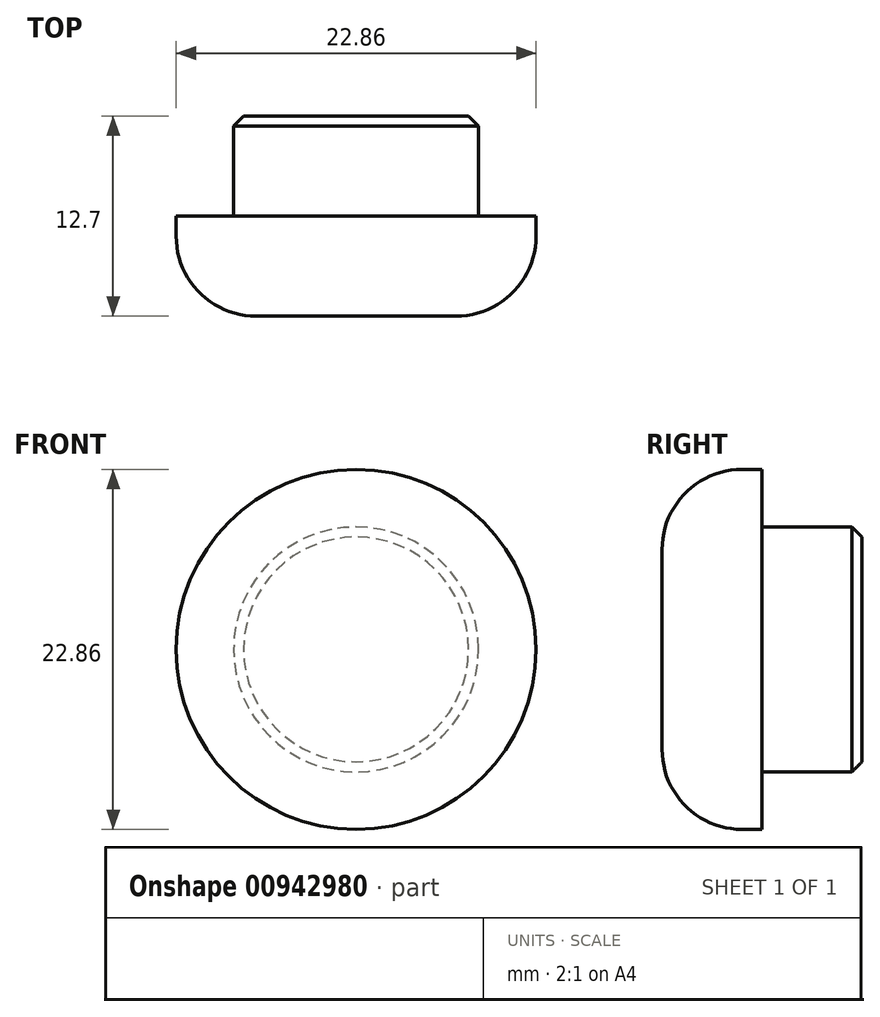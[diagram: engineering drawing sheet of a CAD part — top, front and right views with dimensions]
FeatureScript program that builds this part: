
annotation { "Feature Type Name" : "Feature", "Feature Type Description" : "" }
export const myFeature = defineFeature(function(context is Context, id is Id, definition is map)
    precondition{}
    {
        {
            var Q0;
            Q0=qCreatedBy(makeId("Front.planeOp"),FACE);
            var sketch = newSketch(context, id + "F0", { "sketchPlane" : qUnion([Q0])});
            skCircle(sketch, "E0", {"center": v(25.48, 31.94) * mm, "radius": 7.78 * mm});
            skLineSegment(sketch, "E1", {"start": v(25.48, 31.94) * mm, "end": v(25.48, 39.72) * mm});
            skLineSegment(sketch, "E2", {"start": v(25.48, 39.72) * mm, "end": v(25.48, 24.17) * mm});
            skCircle(sketch, "E3", {"center": v(25.48, 31.94) * mm, "radius": 11.43 * mm});
            skLineSegment(sketch, "E4", {"start": v(25.48, 31.94) * mm, "end": v(36.9, 31.94) * mm});
            skLineSegment(sketch, "E5", {"start": v(36.9, 31.94) * mm, "end": v(25.48, 31.94) * mm});
            skLineSegment(sketch, "E6", {"start": v(25.48, 31.94) * mm, "end": v(14.05, 31.94) * mm});
            skSolve(sketch);
        }
        {
            var Q0;
            {var subQ0=sQuery(id+"F0.wireOp",EDGE,"E1");Q0=makeQuery(id+"F0.imprint","IMPRINT",FACE,{"disambiguationData":[TD([[makeQuery(id+"F0.imprint","IMPRINT",EDGE,{"derivedFrom":subQ0}),1.0]])]});}
            var Q1;
            {var subQ0=sQuery(id+"F0.wireOp",EDGE,"E1");Q1=makeQuery(id+"F0.imprint","IMPRINT",FACE,{"disambiguationData":[TD([[makeQuery(id+"F0.imprint","IMPRINT",EDGE,{"derivedFrom":subQ0}),-1.0]])]});}
            var Q2;
            {var subQ0=sQuery(id+"F0.wireOp",EDGE,"E2");Q2=makeQuery(id+"F0.imprint","IMPRINT",FACE,{"disambiguationData":[TD([[makeQuery(id+"F0.imprint","IMPRINT",EDGE,{"derivedFrom":subQ0}),1.0]])]});}
            var Q3;
            {var subQ0=sQuery(id+"F0.wireOp",EDGE,"E2");Q3=makeQuery(id+"F0.imprint","IMPRINT",FACE,{"disambiguationData":[TD([[makeQuery(id+"F0.imprint","IMPRINT",EDGE,{"derivedFrom":subQ0}),-1.0]])]});}
            extrude(context, id + "F1", {"entities" : qUnion([Q0, Q1, Q2, Q3]), "oppositeDirection" : true, "depth" : 6.35 * mm, "offsetDistance" : 25.4 * mm});
        }
        {
            var Q0;
            Q0=makeQuery(id+"F1.opExtrude","CAP_EDGE",EDGE,{"disambiguationData":[OSD([sQuery(id+"F0.wireOp",EDGE,"E0")])],"isStart":false});
            chamfer(context, id + "F2", {"entities" : qUnion([Q0]), "width" : 0.64 * mm, "tangentPropagation" : true});
        }
        {
            var Q0;
            {var subQ3=sQuery(id+"F0.wireOp",EDGE,"E0");var subQ5=makeQuery(id+"F0.imprint","INTERSECT",VERTEX,{"derivedFrom":[subQ3,sQuery(id+"F0.wireOp",EDGE,"E1")]});Q0=makeQuery(id+"F0.imprint","IMPRINT",FACE,{"disambiguationData":[TD([[makeQuery(id+"F0.imprint","IMPRINT",EDGE,{"disambiguationData":[TD([[subQ5,1.0]])],"derivedFrom":subQ3}),-1.0]])]});}
            var Q1;
            {var subQ3=sQuery(id+"F0.wireOp",EDGE,"E0");var subQ7=makeQuery(id+"F0.imprint","INTERSECT",VERTEX,{"derivedFrom":[subQ3,sQuery(id+"F0.wireOp",EDGE,"E2")]});Q1=makeQuery(id+"F0.imprint","IMPRINT",FACE,{"disambiguationData":[TD([[makeQuery(id+"F0.imprint","IMPRINT",EDGE,{"disambiguationData":[TD([[subQ7,-1.0]])],"derivedFrom":subQ3}),-1.0]])]});}
            var Q2;
            Q2=makeQuery(id+"F1.opExtrude","CAP_FACE",FACE,{"disambiguationData":[OSD([sQuery(id+"F0.wireOp",EDGE,"E0")])],"isStart":true});
            extrude(context, id + "F3", {"entities" : qUnion([Q0, Q1, Q2]), "operationType" : NewBodyOperationType.ADD, "depth" : 6.35 * mm, "offsetDistance" : 25.4 * mm});
        }
        {
            var Q0;
            Q0=makeQuery(id+"F3.opExtrude","CAP_EDGE",EDGE,{"disambiguationData":[OSD([sQuery(id+"F0.wireOp",EDGE,"E3")])],"isStart":false});
            fillet(context, id + "F4", {"entities" : qUnion([Q0]), "radius" : 5.08 * mm, "tangentPropagation" : true, "allowEdgeOverflow" : false});
        }
    });
